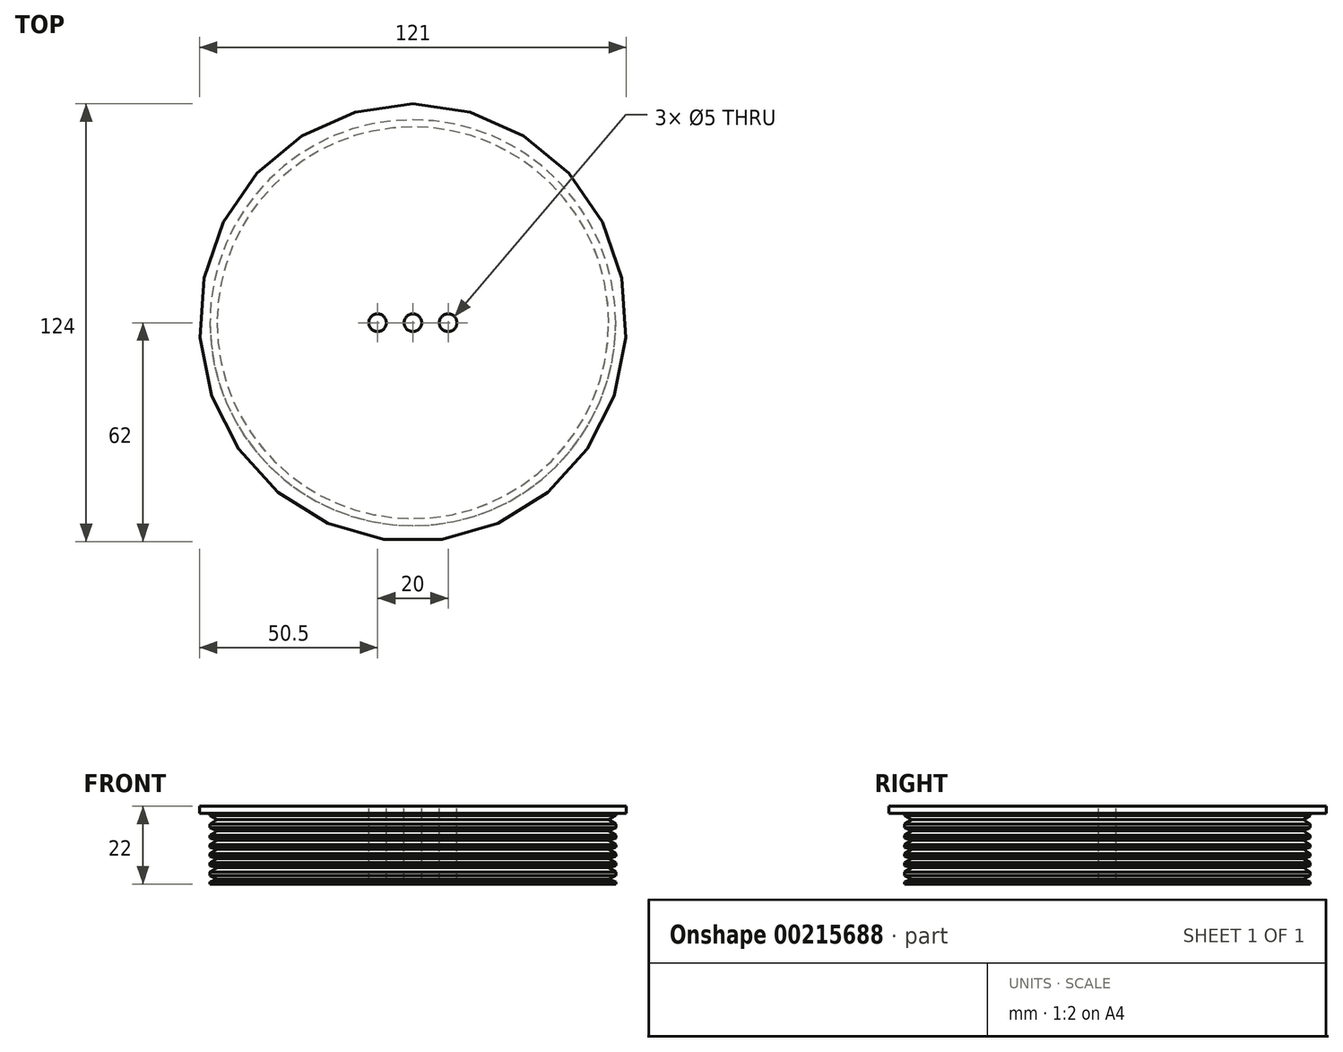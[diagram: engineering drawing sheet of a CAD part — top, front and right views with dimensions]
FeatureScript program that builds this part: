
annotation { "Feature Type Name" : "Feature", "Feature Type Description" : "" }
export const myFeature = defineFeature(function(context is Context, id is Id, definition is map)
    precondition{}
    {
        {
            var Q0;
            Q0=qCreatedBy(makeId("Top.planeOp"),FACE);
            var sketch = newSketch(context, id + "F0", { "sketchPlane" : qUnion([Q0])});
            skCircle(sketch, "E0", {"center": v(0, 0) * mm, "radius": 57.5 * mm});
            skSolve(sketch);
        }
        {
            var Q0;
            Q0 = qSketchRegion(id + "F0", true);
            extrude(context, id + "F1", {"entities" : qUnion([Q0]), "depth" : 20 * mm});
        }
        {
            var Q0;
            Q0=makeQuery(id+"F1.opExtrude","CAP_FACE",FACE,{"disambiguationData":[OSD([sQuery(id+"F0.wireOp",EDGE,"E0")])],"isStart":false});
            var sketch = newSketch(context, id + "F2", { "sketchPlane" : qUnion([Q0])});
            skEllipse(sketch, "E1", {"center": v(0, 0) * mm, "majorRadius": 62 * mm, "minorRadius": 60.5 * mm, "majorAxis": v(0, 1)});
            skSolve(sketch);
        }
        {
            var Q0;
            Q0 = qSketchRegion(id + "F2", true);
            extrude(context, id + "F3", {"entities" : qUnion([Q0]), "operationType" : NewBodyOperationType.ADD, "depth" : 2 * mm});
        }
        {
            var Q0;
            Q0=makeQuery(id+"F3.opExtrude","CAP_FACE",FACE,{"disambiguationData":[OSD([sQuery(id+"F2.wireOp",EDGE,"E1")])],"isStart":false});
            var sketch = newSketch(context, id + "F4", { "sketchPlane" : qUnion([Q0])});
            skCircle(sketch, "E2", {"center": v(0, 0) * mm, "radius": 2.5 * mm});
            skCircle(sketch, "E3", {"center": v(10, 0) * mm, "radius": 2.5 * mm});
            skCircle(sketch, "E4.MirrorC", {"center": v(-10, 0) * mm, "radius": 2.5 * mm});
            skSolve(sketch);
        }
        {
            var Q0;
            Q0 = qSketchRegion(id + "F4", true);
            extrude(context, id + "F5", {"entities" : qUnion([Q0]), "operationType" : NewBodyOperationType.REMOVE, "endBound" : BoundingType.THROUGH_ALL, "oppositeDirection" : true, "depth" : 25 * mm});
        }
        {
            var Q0;
            Q0=qCreatedBy(makeId("Front.planeOp"),FACE);
            var sketch = newSketch(context, id + "F6", { "sketchPlane" : qUnion([Q0])});
            skLineSegment(sketch, "E5", {"start": v(58.4, 19.9) * mm, "end": v(55.48, 18.26) * mm});
            skLineSegment(sketch, "E6", {"start": v(55.48, 18.26) * mm, "end": v(58.4, 16.33) * mm});
            skLineSegment(sketch, "E7", {"start": v(58.4, 16.33) * mm, "end": v(55.48, 15.01) * mm});
            skLineSegment(sketch, "E8", {"start": v(55.48, 15.01) * mm, "end": v(58.4, 13.23) * mm});
            skLineSegment(sketch, "E9", {"start": v(58.4, 13.23) * mm, "end": v(55.48, 12.39) * mm});
            skLineSegment(sketch, "E10", {"start": v(55.48, 12.39) * mm, "end": v(58.4, 10.6) * mm});
            skLineSegment(sketch, "E11", {"start": v(58.4, 10.6) * mm, "end": v(55.48, 9.86) * mm});
            skLineSegment(sketch, "E12", {"start": v(55.48, 9.86) * mm, "end": v(58.4, 8.08) * mm});
            skLineSegment(sketch, "E13", {"start": v(58.4, 8.08) * mm, "end": v(55.48, 7.23) * mm});
            skLineSegment(sketch, "E14", {"start": v(55.48, 7.23) * mm, "end": v(58.4, 5.45) * mm});
            skLineSegment(sketch, "E15", {"start": v(58.4, 5.45) * mm, "end": v(55.48, 4.6) * mm});
            skLineSegment(sketch, "E16", {"start": v(55.48, 4.6) * mm, "end": v(58.4, 2.85) * mm});
            skLineSegment(sketch, "E17", {"start": v(58.4, 2.85) * mm, "end": v(55.48, 1.35) * mm});
            skLineSegment(sketch, "E18", {"start": v(55.48, 1.35) * mm, "end": v(58.96, 0) * mm});
            skLineSegment(sketch, "E19", {"start": v(58.96, 0) * mm, "end": v(68.93, 0) * mm});
            skLineSegment(sketch, "E20", {"start": v(68.93, 0) * mm, "end": v(68.93, 19.9) * mm});
            skLineSegment(sketch, "E21", {"start": v(58.4, 19.9) * mm, "end": v(68.93, 19.9) * mm});
            skLineSegment(sketch, "E22", {"start": v(0, 37.84) * mm, "end": v(0, -20.47) * mm, "construction": true});
            skSolve(sketch);
        }
        {
            var Q0;
            Q0=makeQuery(id+"F6.imprint","IMPRINT",FACE,{"disambiguationData":[TD([[makeQuery(id+"F6.imprint","IMPRINT",EDGE,{"derivedFrom":sQuery(id+"F6.wireOp",EDGE,"E5")}),1.0]])]});
            var Q1;
            Q1=sQuery(id+"F6.wireOp",EDGE,"E22");
            revolve(context, id + "F7", {"operationType" : NewBodyOperationType.REMOVE, "entities" : qUnion([Q0]), "axis" : qUnion([Q1]), "revolveType" : RevolveType.FULL, "oppositeDirection" : true});
        }
    });
